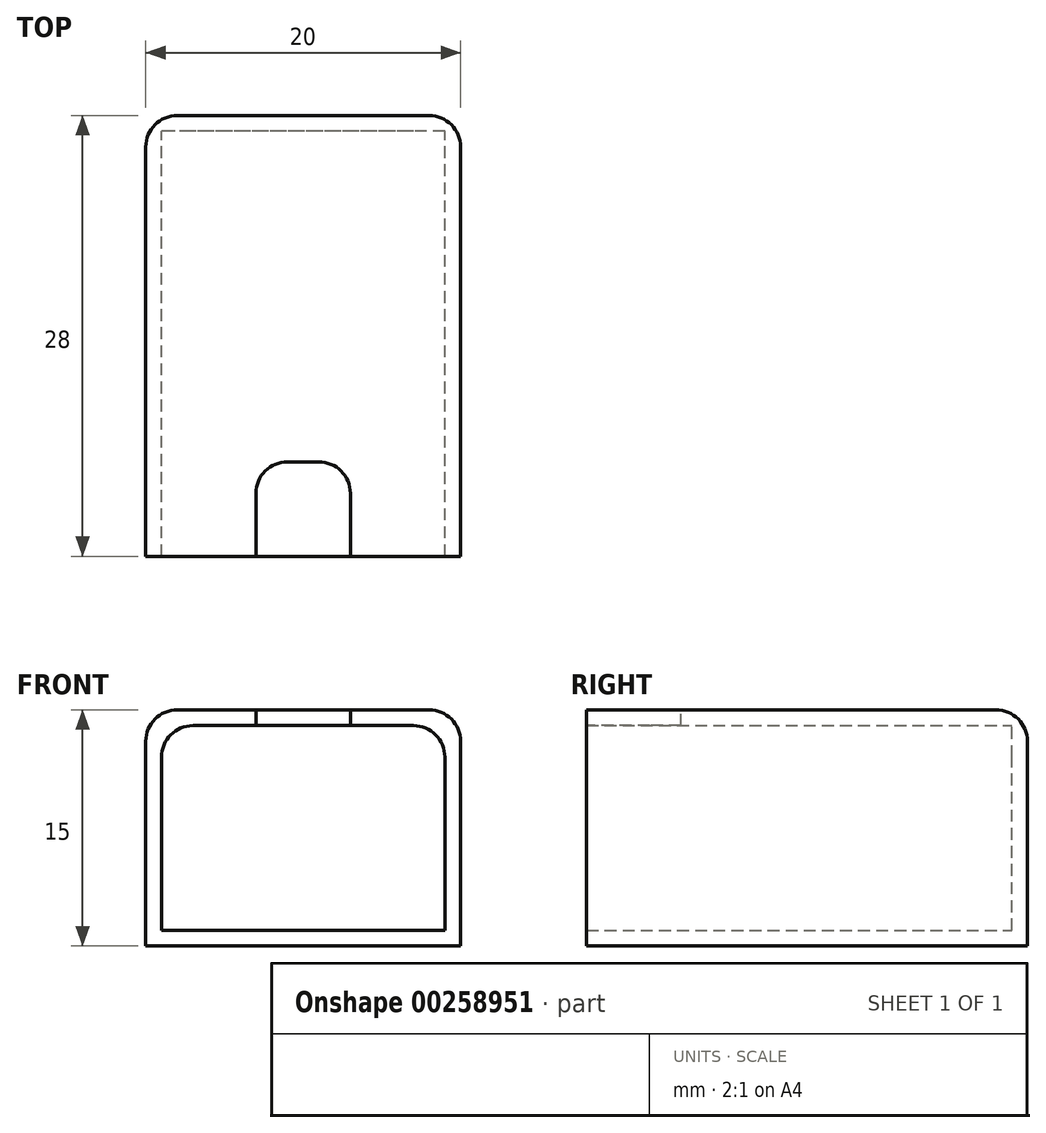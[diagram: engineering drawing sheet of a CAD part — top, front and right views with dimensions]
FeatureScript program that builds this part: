
annotation { "Feature Type Name" : "Feature", "Feature Type Description" : "" }
export const myFeature = defineFeature(function(context is Context, id is Id, definition is map)
    precondition{}
    {
        {
            var Q0;
            Q0=qCreatedBy(makeId("Front.planeOp"),FACE);
            var sketch = newSketch(context, id + "F0", { "sketchPlane" : qUnion([Q0])});
            skLineSegment(sketch, "E0.bottom", {"start": v(10, -7.5) * mm, "end": v(-10, -7.5) * mm});
            skLineSegment(sketch, "E0.top", {"start": v(10, 7.5) * mm, "end": v(-10, 7.5) * mm});
            skLineSegment(sketch, "E0.left", {"start": v(10, -7.5) * mm, "end": v(10, 7.5) * mm});
            skLineSegment(sketch, "E0.right", {"start": v(-10, -7.5) * mm, "end": v(-10, 7.5) * mm});
            skPoint(sketch, "E0.middle", {"position": v(0, 0) * mm});
            skSolve(sketch);
        }
        {
            var Q0;
            Q0=makeQuery(id+"F0.imprint","IMPRINT",FACE,{"disambiguationData":[TD([[makeQuery(id+"F0.imprint","IMPRINT",EDGE,{"derivedFrom":sQuery(id+"F0.wireOp",EDGE,"E0.bottom")}),-1.0]])]});
            extrude(context, id + "F1", {"entities" : qUnion([Q0]), "depth" : (26 + 2) * mm});
        }
        {
            var Q0;
            Q0=makeQuery(id+"F1.opExtrude","CAP_FACE",FACE,{"disambiguationData":[OSD([sQuery(id+"F0.wireOp",EDGE,"E0.bottom"),sQuery(id+"F0.wireOp",EDGE,"E0.top"),sQuery(id+"F0.wireOp",EDGE,"E0.left"),sQuery(id+"F0.wireOp",EDGE,"E0.right")])],"isStart":false});
            shell(context, id + "F2", {"entities" : qUnion([Q0]), "thickness" : 1 * mm});
        }
        {
            var Q0;
            Q0=makeQuery(id+"F2.opShell","OFFSET_EDGE",EDGE,{"disambiguationData":[OSD([sQuery(id+"F0.wireOp",EDGE,"E0.top"),sQuery(id+"F0.wireOp",EDGE,"E0.right")])]});
            var Q1;
            Q1=makeQuery(id+"F2.opShell","OFFSET_EDGE",EDGE,{"disambiguationData":[OSD([sQuery(id+"F0.wireOp",EDGE,"E0.top"),sQuery(id+"F0.wireOp",EDGE,"E0.left")])]});
            fillet(context, id + "F3", {"entities" : qUnion([Q0, Q1]), "radius" : 2 * mm, "tangentPropagation" : true, "allowEdgeOverflow" : false});
        }
        {
            var Q0;
            Q0=makeQuery(id+"F1.opExtrude","SWEPT_EDGE",EDGE,{"disambiguationData":[OSD([sQuery(id+"F0.wireOp",EDGE,"E0.top"),sQuery(id+"F0.wireOp",EDGE,"E0.left")])]});
            var Q1;
            Q1=makeQuery(id+"F1.opExtrude","SWEPT_EDGE",EDGE,{"disambiguationData":[OSD([sQuery(id+"F0.wireOp",EDGE,"E0.top"),sQuery(id+"F0.wireOp",EDGE,"E0.right")])]});
            fillet(context, id + "F4", {"entities" : qUnion([Q0, Q1]), "radius" : 2 * mm, "tangentPropagation" : true, "allowEdgeOverflow" : false});
        }
        {
            var Q0;
            Q0=makeQuery(id+"F1.opExtrude","CAP_EDGE",EDGE,{"disambiguationData":[OSD([sQuery(id+"F0.wireOp",EDGE,"E0.top")])],"isStart":true});
            var Q1;
            Q1=makeQuery(id+"F1.opExtrude","CAP_EDGE",EDGE,{"disambiguationData":[OSD([sQuery(id+"F0.wireOp",EDGE,"E0.left")])],"isStart":true});
            var Q2;
            Q2=makeQuery(id+"F1.opExtrude","CAP_EDGE",EDGE,{"disambiguationData":[OSD([sQuery(id+"F0.wireOp",EDGE,"E0.right")])],"isStart":true});
            fillet(context, id + "F5", {"entities" : qUnion([Q0, Q1, Q2]), "radius" : 2 * mm, "tangentPropagation" : true, "allowEdgeOverflow" : false});
        }
        {
            var Q0;
            Q0=makeQuery(id+"F1.opExtrude","SWEPT_FACE",FACE,{"disambiguationData":[OSD([sQuery(id+"F0.wireOp",EDGE,"E0.top")])]});
            var sketch = newSketch(context, id + "F6", { "sketchPlane" : qUnion([Q0])});
            skLineSegment(sketch, "E1", {"start": v(0, -28) * mm, "end": v(0, -24.15) * mm});
            skPoint(sketch, "E1.endSnap0", {"position": v(0, -28) * mm});
            skLineSegment(sketch, "E2.bottom", {"start": v(3, -22) * mm, "end": v(-3, -22) * mm});
            skLineSegment(sketch, "E2.top", {"start": v(3, -34) * mm, "end": v(-3, -34) * mm});
            skLineSegment(sketch, "E2.left", {"start": v(3, -22) * mm, "end": v(3, -34) * mm});
            skLineSegment(sketch, "E2.right", {"start": v(-3, -22) * mm, "end": v(-3, -34) * mm});
            skSolve(sketch);
        }
        {
            var Q0;
            {var subQ5=sQuery(id+"F6.wireOp",EDGE,"E2.bottom");Q0=makeQuery(id+"F6.imprint","IMPRINT",FACE,{"disambiguationData":[TD([[makeQuery(id+"F6.imprint","IMPRINT",EDGE,{"derivedFrom":subQ5}),1.0]])]});}
            extrude(context, id + "F7", {"entities" : qUnion([Q0]), "operationType" : NewBodyOperationType.REMOVE, "endBound" : BoundingType.UP_TO_NEXT, "oppositeDirection" : true, "depth" : 25 * mm});
        }
        {
            var Q0;
            Q0=makeQuery(id+"F7.boolean.opBoolean","COPY",EDGE,{"derivedFrom":makeQuery(id+"F7.opExtrude","SWEPT_EDGE",EDGE,{"disambiguationData":[OSD([sQuery(id+"F6.wireOp",EDGE,"E2.bottom"),sQuery(id+"F6.wireOp",EDGE,"E2.right")])]})});
            var Q1;
            Q1=makeQuery(id+"F7.boolean.opBoolean","COPY",EDGE,{"derivedFrom":makeQuery(id+"F7.opExtrude","SWEPT_EDGE",EDGE,{"disambiguationData":[OSD([sQuery(id+"F6.wireOp",EDGE,"E2.bottom"),sQuery(id+"F6.wireOp",EDGE,"E2.left")])]})});
            fillet(context, id + "F8", {"entities" : qUnion([Q0, Q1]), "radius" : 2 * mm, "tangentPropagation" : true, "allowEdgeOverflow" : false});
        }
    });
